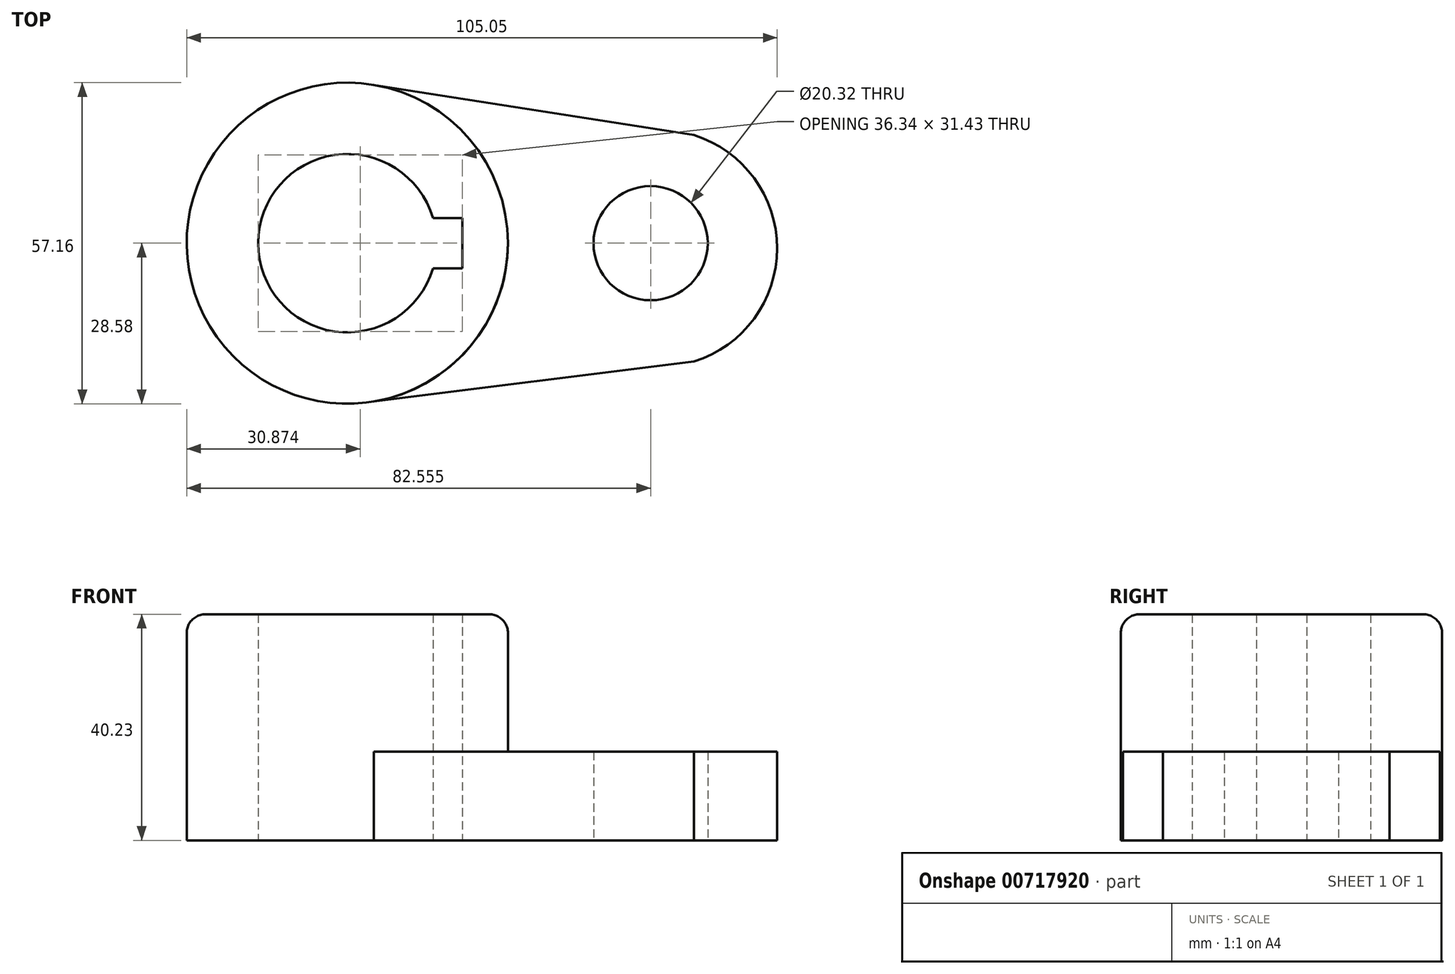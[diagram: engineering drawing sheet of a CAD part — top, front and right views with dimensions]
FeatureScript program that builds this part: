
annotation { "Feature Type Name" : "Feature", "Feature Type Description" : "" }
export const myFeature = defineFeature(function(context is Context, id is Id, definition is map)
    precondition{}
    {
        {
            var Q0;
            Q0=qCreatedBy(makeId("Top.planeOp"),FACE);
            var sketch = newSketch(context, id + "F0", { "sketchPlane" : qUnion([Q0])});
            skArc(sketch, "E0", {"start": v(15.23, 4.48) * mm, "mid": v(-15.87, 0) * mm, "end": v(15.23, -4.48) * mm});
            skLineSegment(sketch, "E1", {"start": v(20.46, 4.48) * mm, "end": v(20.46, -4.48) * mm});
            skLineSegment(sketch, "E2", {"start": v(20.46, -4.48) * mm, "end": v(15.23, -4.48) * mm});
            skLineSegment(sketch, "E3", {"start": v(20.46, 4.48) * mm, "end": v(15.23, 4.48) * mm});
            skCircle(sketch, "E4", {"center": v(0, 0) * mm, "radius": 28.58 * mm});
            skLineSegment(sketch, "E5", {"start": v(4.74, 28.18) * mm, "end": v(61.7, 19.24) * mm});
            skLineSegment(sketch, "E6", {"start": v(4.74, -28.18) * mm, "end": v(61.7, -21.08) * mm});
            skArc(sketch, "E7", {"start": v(61.7, -21.08) * mm, "mid": v(76.47, -0.92) * mm, "end": v(61.7, 19.24) * mm});
            skSolve(sketch);
        }
        {
            var Q0;
            Q0=qCreatedBy(makeId("Top.planeOp"),FACE);
            var sketch = newSketch(context, id + "F1", { "sketchPlane" : qUnion([Q0])});
            skCircle(sketch, "E8", {"center": v(53.98, 0) * mm, "radius": 10.16 * mm});
            skSolve(sketch);
        }
        {
            var Q0;
            Q0=makeQuery(id+"F0.imprint","IMPRINT",FACE,{"disambiguationData":[TD([[makeQuery(id+"F0.imprint","IMPRINT",EDGE,{"derivedFrom":sQuery(id+"F0.wireOp",EDGE,"E0")}),-1.0]])]});
            extrude(context, id + "F2", {"entities" : qUnion([Q0]), "depth" : 40.23 * mm, "offsetDistance" : 25.4 * mm});
        }
        {
            var Q0;
            {var subQ0=sQuery(id+"F0.wireOp",EDGE,"E5");Q0=makeQuery(id+"F0.imprint","IMPRINT",FACE,{"disambiguationData":[TD([[makeQuery(id+"F0.imprint","IMPRINT",EDGE,{"derivedFrom":subQ0}),-1.0]])]});}
            extrude(context, id + "F3", {"entities" : qUnion([Q0]), "operationType" : NewBodyOperationType.ADD, "depth" : 15.77 * mm, "offsetDistance" : 25.4 * mm});
        }
        {
            var Q0;
            Q0=makeQuery(id+"F2.opExtrude","CAP_EDGE",EDGE,{"disambiguationData":[OSD([sQuery(id+"F0.wireOp",EDGE,"E4")])],"isStart":false});
            fillet(context, id + "F4", {"entities" : qUnion([Q0]), "radius" : 3.3 * mm, "tangentPropagation" : true, "allowEdgeOverflow" : false});
        }
        {
            var Q0;
            Q0=makeQuery(id+"F1.imprint","IMPRINT",FACE,{"disambiguationData":[TD([[makeQuery(id+"F1.imprint","IMPRINT",EDGE,{"derivedFrom":sQuery(id+"F1.wireOp",EDGE,"E8")}),1.0]])]});
            extrude(context, id + "F5", {"entities" : qUnion([Q0]), "operationType" : NewBodyOperationType.REMOVE, "depth" : 40.64 * mm, "offsetDistance" : 25.4 * mm});
        }
    });
